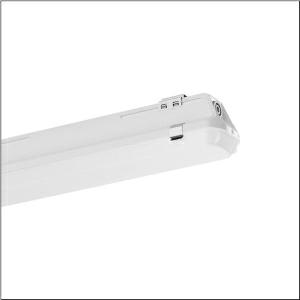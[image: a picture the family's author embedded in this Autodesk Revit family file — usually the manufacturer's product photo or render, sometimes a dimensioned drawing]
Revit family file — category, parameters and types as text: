
# Revit family: monsun_r__21_51fb207p460b005_f6e2
name_source: partatom
category: Lighting Fixtures
units: mm (PartAtom-declared; Revit-internal decimal feet)

## family parameters
Cut with Voids When Loaded = No
Host = Face
Light Source = No
Part Type = Normal
Room Calculation Point = No
Round Connector Dimension = Use Diameter
Shared = No

## types (1)
- Monsun® 21 (1 x LED, 5400 lm, 38 W, 4000K)
    Apparent Load = 38 VA
    CIE Flux Codes = 45 75 93 94 100
    Color Rendering = 80
    Color Temperature = 4000K
    Default Elevation = 1800 mm
    Description = Monsun® 21, damp-proof luminaire, chain hanger, primary optical cover: enclosure, of PC, light emission: direct distribution, primary light characteristic: symmetric, installation type: suspended mounting, surface-mounted, horizontal mounting, vertical mounting, LED, rated luminous flux: 5.400lm, luminous efficacy: 142lm/W, light colour: 840, colour temperature: 4000K, control gear: ECG, with terminal, 3-pole, max. 2.5mm², through-wiring: 5x 2.5mm², mains connection: 220..240V, AC, 50/60Hz, rated input power: 38W, housing, of glass-fibre reinforced polyester, uncoated, bright grey, incl. chain hanger, length: 1.590mm, width: 90mm, height: 88mm, clip for enclosure, of stainless steel (V2A), ceiling mounting element, of stainless steel (V2A), chain hanger, of stainless steel (V2A), protection rating (complete): IP66, insulation class (complete): insulation class I (protective earthing), certification: CE, ENEC, VDE, UKCA, protection symbol: D, impact resistance: IK08, permissible operating ambient temperature: -25..+35°C, standard: EN 50419, EN 60598-2-1, corresponds to IFS (International Featured Standards) requirements for safety and quality in the food industry, for indoor or canopied outdoor use, no direct snow, no direct sun, no direct rain, contact your sales advisor before using the luminaires in applications with unclear chemical exposure, large temperature fluctuations or condensation-forming humidity, LABS conformity tested according to VDMA 24364:2018-05, packaging unit: 1 piece
    Height = 89 mm
    Lamp = 1 x LED
    Lamp Light Flux = 5400 lm
    Lamp Power = 38 W
    Lamp count = 1
    Length = 1590 mm
    Luminous efficacy = 142 lm/W
    Manufacturer = Siteco
    ModVariant = No
    Model = 51FB207P460B005
    Mounting Place = Ceiling
    Mounting Type = Surface mounted
    Number of Poles = 1
    OnlyDefault = Yes
    Power Factor = 1
    Product Name = Monsun® 21
    Product group = damp-proof luminaire
    ProductGroupID = 300
    Protection Class = Protection class I
    Protection Degree = IP 66
    RLX_Detail_Level = 1
    RLX_Emergency_Light_Flux = 0 lm
    RLX_Emergency_Type = 0
    RLX_Emergency_Type_DB = No
    RlxData = <blob elided: 88893 chars, md5=81e148ed>
    Socket = socket
    Standby Power = 0 W
    System Light Flux = 5400 lm
    System Power = 38 W
    Type Comments = Product without accessories
    Type Image = l_1006717.jpg
    URL = http://relux.com
    VarID = ---
    Voltage = 0 V
    Weight = 0.00 kg
    Width = 90 mm

## geometry (parser evidence)
native form markers: Blend x4, Sweep x12
no freeform markers — native parametric forms only
